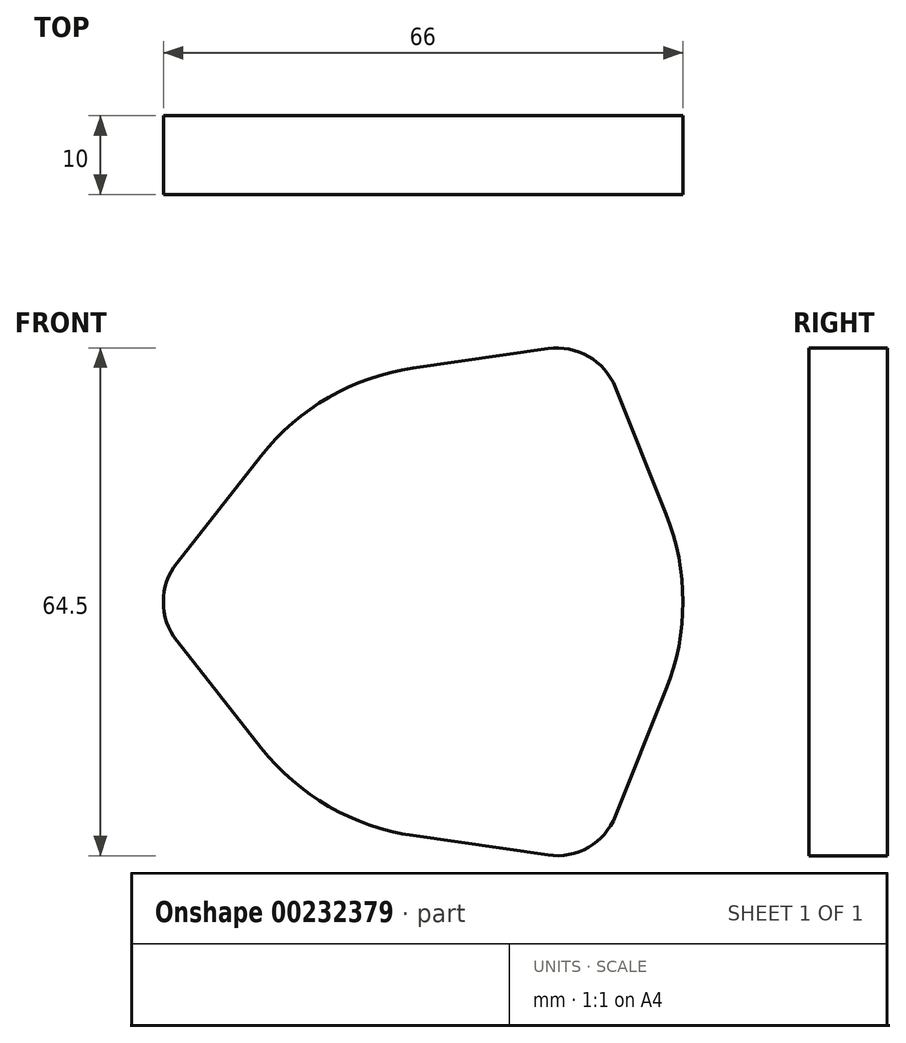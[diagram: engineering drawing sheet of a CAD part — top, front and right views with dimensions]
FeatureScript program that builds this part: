
annotation { "Feature Type Name" : "Feature", "Feature Type Description" : "" }
export const myFeature = defineFeature(function(context is Context, id is Id, definition is map)
    precondition{}
    {
        {
            var Q0;
            Q0=qCreatedBy(makeId("Front.planeOp"),FACE);
            var sketch = newSketch(context, id + "F0", { "sketchPlane" : qUnion([Q0])});
            skArc(sketch, "E0", {"start": v(-23.57, -18.56) * mm, "mid": v(-15, -25.98) * mm, "end": v(-4.29, -29.7) * mm});
            skCircle(sketch, "E1", {"center": v(0, 0) * mm, "radius": 28 * mm, "construction": true});
            skArc(sketch, "E2", {"start": v(-34.29, 4.95) * mm, "mid": v(-36, 0) * mm, "end": v(-34.29, -4.95) * mm});
            skLineSegment(sketch, "E3", {"start": v(-34.29, -4.95) * mm, "end": v(-23.57, -18.56) * mm});
            skPoint(sketch, "E4.orphan", {"position": v(-30.6, -7.57) * mm});
            skLineSegment(sketch, "E5", {"start": v(-23.57, 18.56) * mm, "end": v(-34.29, 4.95) * mm});
            skPoint(sketch, "E6.orphan", {"position": v(-31.72, 7.08) * mm});
            skLineSegment(sketch, "E7.1.0", {"start": v(-4.29, -29.7) * mm, "end": v(12.86, -32.17) * mm});
            skArc(sketch, "E7.1.1", {"start": v(12.86, -32.17) * mm, "mid": v(18, -31.18) * mm, "end": v(21.43, -27.22) * mm});
            skLineSegment(sketch, "E7.1.2", {"start": v(21.43, -27.22) * mm, "end": v(27.86, -11.13) * mm});
            skLineSegment(sketch, "E7.2.0", {"start": v(27.86, 11.13) * mm, "end": v(21.43, 27.22) * mm});
            skArc(sketch, "E7.2.1", {"start": v(21.43, 27.22) * mm, "mid": v(18, 31.18) * mm, "end": v(12.86, 32.17) * mm});
            skLineSegment(sketch, "E7.2.2", {"start": v(12.86, 32.17) * mm, "end": v(-4.29, 29.7) * mm});
            skArc(sketch, "E8.trimOffspring", {"start": v(-4.29, 29.7) * mm, "mid": v(-15, 25.98) * mm, "end": v(-23.57, 18.56) * mm});
            skArc(sketch, "E9.trimOffspring", {"start": v(27.86, -11.13) * mm, "mid": v(30, 0) * mm, "end": v(27.86, 11.13) * mm});
            skSolve(sketch);
        }
        {
            var Q0;
            Q0=makeQuery(id+"F0.imprint","IMPRINT",FACE,{"disambiguationData":[TD([[makeQuery(id+"F0.imprint","IMPRINT",EDGE,{"derivedFrom":sQuery(id+"F0.wireOp",EDGE,"E0")}),1.0]])]});
            extrude(context, id + "F1", {"entities" : qUnion([Q0]), "depth" : 10 * mm});
        }
    });
